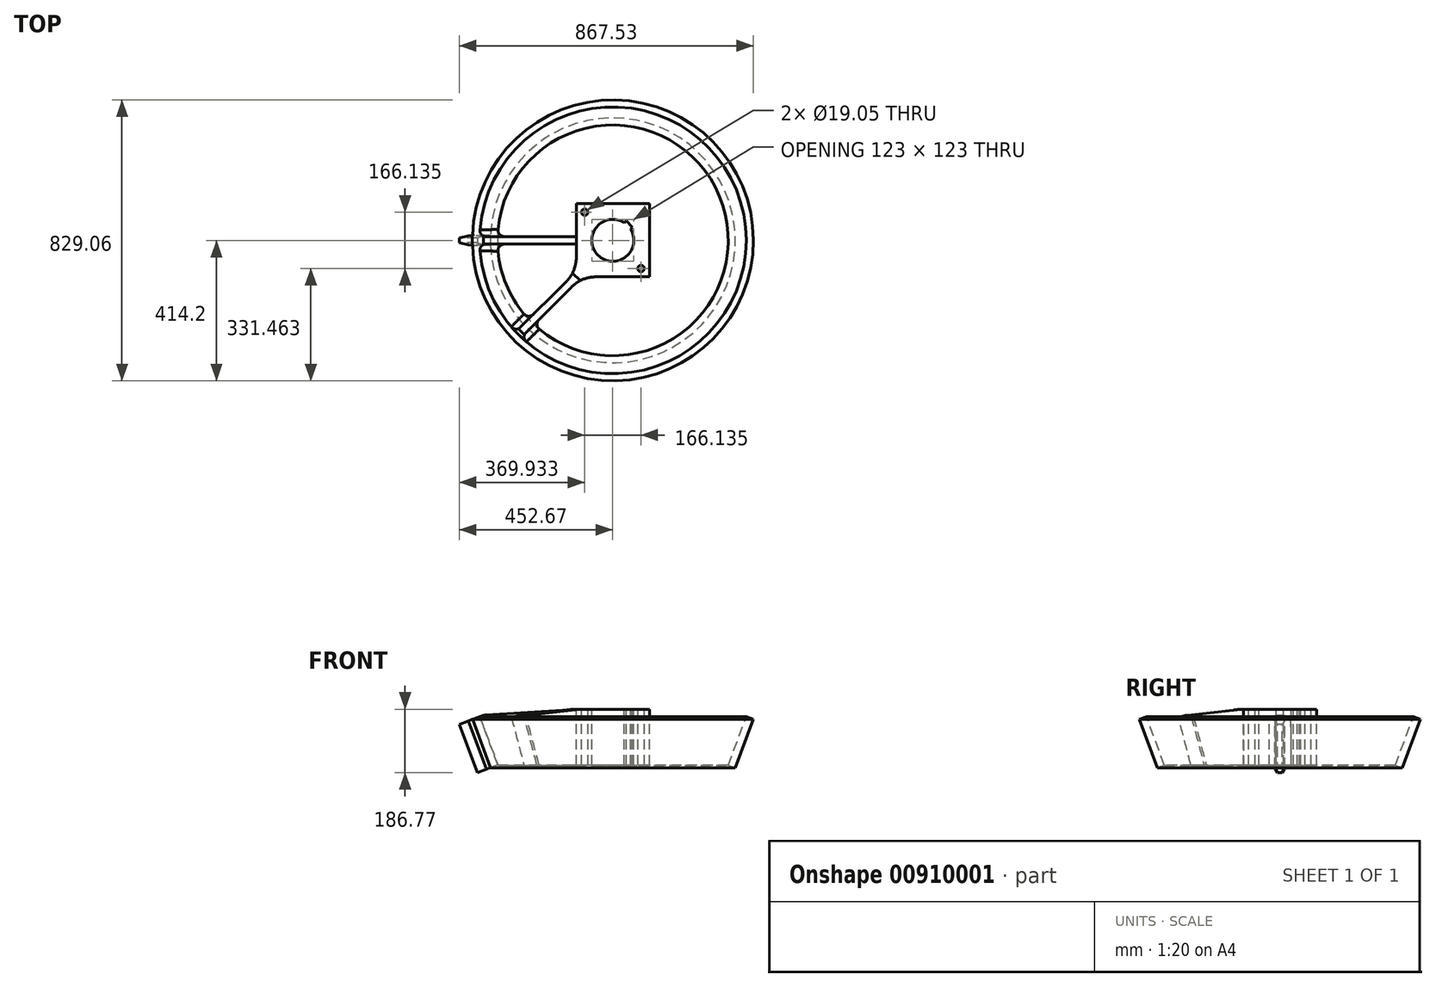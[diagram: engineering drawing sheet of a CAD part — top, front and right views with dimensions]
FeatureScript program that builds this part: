
annotation { "Feature Type Name" : "Feature", "Feature Type Description" : "" }
export const myFeature = defineFeature(function(context is Context, id is Id, definition is map)
    precondition{}
    {
        {
            var Q0;
            Q0=qCreatedBy(makeId("Front.planeOp"),FACE);
            var sketch = newSketch(context, id + "F0", { "sketchPlane" : qUnion([Q0])});
            skLineSegment(sketch, "E0.bottom", {"start": v(107.95, 0) * mm, "end": v(61.91, 0) * mm});
            skLineSegment(sketch, "E0.top", {"start": v(107.95, 165.1) * mm, "end": v(61.91, 165.1) * mm});
            skLineSegment(sketch, "E0.left", {"start": v(107.95, 0) * mm, "end": v(107.95, 165.1) * mm});
            skLineSegment(sketch, "E0.right", {"start": v(-107.95, 0) * mm, "end": v(-107.95, 165.1) * mm});
            skLineSegment(sketch, "E1", {"start": v(61.91, 165.1) * mm, "end": v(61.91, 0) * mm});
            skLineSegment(sketch, "E2", {"start": v(0, 165.1) * mm, "end": v(-107.95, 165.1) * mm});
            skLineSegment(sketch, "E3", {"start": v(61.91, 165.1) * mm, "end": v(0, 165.1) * mm});
            skLineSegment(sketch, "E4", {"start": v(-340.6, 0) * mm, "end": v(-393.7, 142.85) * mm});
            skLineSegment(sketch, "E5", {"start": v(-393.7, 142.85) * mm, "end": v(-414.53, 135.1) * mm});
            skLineSegment(sketch, "E6", {"start": v(-414.53, 135.1) * mm, "end": v(-361.42, -7.75) * mm});
            skLineSegment(sketch, "E7", {"start": v(-361.42, -7.75) * mm, "end": v(-340.6, 0) * mm});
            skLineSegment(sketch, "E8", {"start": v(0, 0) * mm, "end": v(0, 165.1) * mm, "construction": true});
            skLineSegment(sketch, "E9", {"start": v(-340.6, 0) * mm, "end": v(-107.95, 0) * mm});
            skLineSegment(sketch, "E10", {"start": v(-393.7, 142.85) * mm, "end": v(-381.8, 147.27) * mm});
            skLineSegment(sketch, "E11", {"start": v(-381.8, 147.27) * mm, "end": v(-107.95, 165.1) * mm});
            skLineSegment(sketch, "E12", {"start": v(-381.8, 147.27) * mm, "end": v(-386.22, 159.18) * mm});
            skLineSegment(sketch, "E13", {"start": v(-386.22, 159.18) * mm, "end": v(-418.96, 147) * mm});
            skLineSegment(sketch, "E14", {"start": v(-418.96, 147) * mm, "end": v(-414.53, 135.1) * mm});
            skLineSegment(sketch, "E15", {"start": v(-107.95, 0) * mm, "end": v(0, 0) * mm});
            skLineSegment(sketch, "E16", {"start": v(0, 0) * mm, "end": v(61.91, 0) * mm});
            skLineSegment(sketch, "E17", {"start": v(0, 0) * mm, "end": v(0, 165.1) * mm});
            skSolve(sketch);
        }
        {
            var Q0;
            Q0=makeQuery(id+"F0.imprint","IMPRINT",FACE,{"disambiguationData":[TD([[makeQuery(id+"F0.imprint","IMPRINT",EDGE,{"derivedFrom":sQuery(id+"F0.wireOp",EDGE,"E0.right")}),-1.0]])]});
            var Q1;
            Q1=makeQuery(id+"F0.imprint","IMPRINT",FACE,{"disambiguationData":[TD([[makeQuery(id+"F0.imprint","IMPRINT",EDGE,{"derivedFrom":sQuery(id+"F0.wireOp",EDGE,"E1")}),-1.0]])]});
            var Q2;
            Q2=makeQuery(id+"F0.imprint","IMPRINT",FACE,{"disambiguationData":[TD([[makeQuery(id+"F0.imprint","IMPRINT",EDGE,{"derivedFrom":sQuery(id+"F0.wireOp",EDGE,"E0.bottom")}),-1.0]])]});
            extrude(context, id + "F1", {"entities" : qUnion([Q0, Q1, Q2]), "depth" : 215.9 * mm, "offsetDistance" : 25 * mm, "symmetric" : true});
        }
        {
            var Q0;
            Q0=makeQuery(id+"F0.imprint","IMPRINT",FACE,{"disambiguationData":[TD([[makeQuery(id+"F0.imprint","IMPRINT",EDGE,{"derivedFrom":sQuery(id+"F0.wireOp",EDGE,"E0.right")}),1.0]])]});
            extrude(context, id + "F2", {"entities" : qUnion([Q0]), "operationType" : NewBodyOperationType.ADD, "depth" : 22.23 * mm, "offsetDistance" : 25 * mm, "symmetric" : true});
        }
        {
            var Q0;
            Q0=makeQuery(id+"F0.imprint","IMPRINT",FACE,{"disambiguationData":[TD([[makeQuery(id+"F0.imprint","IMPRINT",EDGE,{"derivedFrom":sQuery(id+"F0.wireOp",EDGE,"E4")}),1.0]])]});
            var Q1;
            Q1=sQuery(id+"F0.wireOp",EDGE,"E8");
            revolve(context, id + "F3", {"operationType" : NewBodyOperationType.ADD, "surfaceOperationType" : NewSurfaceOperationType.NEW, "entities" : qUnion([Q0]), "axis" : qUnion([Q1]), "revolveType" : RevolveType.FULL});
        }
        {
            var Q0;
            Q0=makeQuery(id+"F1.opExtrude","CAP_VERTEX",VERTEX,{"disambiguationData":[OSD([sQuery(id+"F0.wireOp",EDGE,"E0.right"),sQuery(id+"F0.wireOp",EDGE,"E2"),sQuery(id+"F0.wireOp",EDGE,"E11")])],"isStart":false});
            var Q1;
            Q1=makeQuery(id+"F1.opExtrude","CAP_VERTEX",VERTEX,{"disambiguationData":[OSD([sQuery(id+"F0.wireOp",EDGE,"E0.right"),sQuery(id+"F0.wireOp",EDGE,"bd23a387-63c8-4da3-bc8b-55db6ce0ce16"),sQuery(id+"F0.wireOp",EDGE,"E9")])],"isStart":false});
            var Q2;
            Q2=makeQuery(id+"F1.opExtrude","CAP_VERTEX",VERTEX,{"disambiguationData":[OSD([sQuery(id+"F0.wireOp",EDGE,"E0.top"),sQuery(id+"F0.wireOp",EDGE,"E0.left")])],"isStart":true});
            cPlane(context, id + "F4", {"entities" : qUnion([Q0, Q1, Q2]), "cplaneType" : CPlaneType.THREE_POINT, "offset" : 25 * mm, "width" : 150 * mm, "height" : 150 * mm});
        }
        {
            var Q0;
            Q0=qCreatedBy(id+"F4.planeOp",FACE);
            var sketch = newSketch(context, id + "F5", { "sketchPlane" : qUnion([Q0])});
            skLineSegment(sketch, "E18", {"start": v(101.86, 165.1) * mm, "end": v(152.66, 165.1) * mm});
            skLineSegment(sketch, "E19", {"start": v(381.8, 146.57) * mm, "end": v(393.7, 142.14) * mm});
            skLineSegment(sketch, "E20", {"start": v(393.7, 142.14) * mm, "end": v(340.85, 0) * mm});
            skLineSegment(sketch, "E21", {"start": v(340.85, 0) * mm, "end": v(101.86, 0) * mm});
            skLineSegment(sketch, "E22", {"start": v(101.86, 0) * mm, "end": v(101.86, 165.1) * mm});
            skLineSegment(sketch, "E23", {"start": v(152.66, 165.1) * mm, "end": v(381.8, 146.57) * mm});
            skSolve(sketch);
        }
        {
            var Q0;
            Q0=makeQuery(id+"F5.imprint","IMPRINT",FACE,{"disambiguationData":[TD([[makeQuery(id+"F5.imprint","IMPRINT",EDGE,{"derivedFrom":sQuery(id+"F5.wireOp",EDGE,"E18")}),-1.0]])]});
            extrude(context, id + "F6", {"entities" : qUnion([Q0]), "operationType" : NewBodyOperationType.ADD, "depth" : 22.23 * mm, "offsetDistance" : 25 * mm, "symmetric" : true});
        }
        {
            var Q0;
            Q0=makeQuery(id+"F2.opExtrude","CAP_EDGE",EDGE,{"disambiguationData":[OSD([sQuery(id+"F0.wireOp",EDGE,"E0.right")])],"isStart":false});
            var Q1;
            Q1=makeQuery(id+"F2.opExtrude","CAP_EDGE",EDGE,{"disambiguationData":[OSD([sQuery(id+"F0.wireOp",EDGE,"E0.right")])],"isStart":true});
            var Q2;
            {var subQ0=sQuery(id+"F0.wireOp",EDGE,"E4");Q2=makeQuery(id+"F3.boolean.opBoolean","INTERSECT",EDGE,{"derivedFrom":[makeQuery(id+"F2.opExtrude","CAP_FACE",FACE,{"disambiguationData":[OSD([sQuery(id+"F0.wireOp",EDGE,"E0.right"),subQ0,sQuery(id+"F0.wireOp",EDGE,"E9"),sQuery(id+"F0.wireOp",EDGE,"E10"),sQuery(id+"F0.wireOp",EDGE,"E11")])],"isStart":true}),makeQuery(id+"F3.opRevolve","SWEPT_FACE",FACE,{"disambiguationData":[OSD([subQ0])]})]});}
            var Q3;
            {var subQ0=sQuery(id+"F0.wireOp",EDGE,"E4");Q3=makeQuery(id+"F3.boolean.opBoolean","INTERSECT",EDGE,{"derivedFrom":[makeQuery(id+"F2.opExtrude","CAP_FACE",FACE,{"disambiguationData":[OSD([sQuery(id+"F0.wireOp",EDGE,"E0.right"),subQ0,sQuery(id+"F0.wireOp",EDGE,"E9"),sQuery(id+"F0.wireOp",EDGE,"E10"),sQuery(id+"F0.wireOp",EDGE,"E11")])],"isStart":false}),makeQuery(id+"F3.opRevolve","SWEPT_FACE",FACE,{"disambiguationData":[OSD([subQ0])]})]});}
            var Q4;
            Q4=makeQuery(id+"F6.boolean.opBoolean","INTERSECT",EDGE,{"derivedFrom":[makeQuery(id+"F3.opRevolve","SWEPT_FACE",FACE,{"disambiguationData":[OSD([sQuery(id+"F0.wireOp",EDGE,"E4")])]}),makeQuery(id+"F6.opExtrude","CAP_FACE",FACE,{"disambiguationData":[OSD([sQuery(id+"F5.wireOp",EDGE,"E18"),sQuery(id+"F5.wireOp",EDGE,"E19"),sQuery(id+"F5.wireOp",EDGE,"E20"),sQuery(id+"F5.wireOp",EDGE,"E21"),sQuery(id+"F5.wireOp",EDGE,"E22"),sQuery(id+"F5.wireOp",EDGE,"E23")])],"isStart":false})]});
            var Q5;
            Q5=makeQuery(id+"F6.boolean.opBoolean","INTERSECT",EDGE,{"derivedFrom":[makeQuery(id+"F3.opRevolve","SWEPT_FACE",FACE,{"disambiguationData":[OSD([sQuery(id+"F0.wireOp",EDGE,"E4")])]}),makeQuery(id+"F6.opExtrude","CAP_FACE",FACE,{"disambiguationData":[OSD([sQuery(id+"F5.wireOp",EDGE,"E18"),sQuery(id+"F5.wireOp",EDGE,"E19"),sQuery(id+"F5.wireOp",EDGE,"E20"),sQuery(id+"F5.wireOp",EDGE,"E21"),sQuery(id+"F5.wireOp",EDGE,"E22"),sQuery(id+"F5.wireOp",EDGE,"E23")])],"isStart":true})]});
            var Q6;
            {var subQ0=sQuery(id+"F5.wireOp",EDGE,"E21");var subQ2=sQuery(id+"F0.wireOp",EDGE,"E9");var subQ9=sQuery(id+"F0.wireOp",EDGE,"E11");var subQ10=sQuery(id+"F0.wireOp",EDGE,"E10");var subQ11=sQuery(id+"F0.wireOp",EDGE,"E4");var subQ12=sQuery(id+"F0.wireOp",EDGE,"E0.right");var subQ13=makeQuery(id+"F2.opExtrude","CAP_FACE",FACE,{"disambiguationData":[OSD([subQ12,subQ11,subQ2,subQ10,subQ9])],"isStart":true});Q6=makeQuery(id+"FeQxwqO8TE0xPhn_1.3.F6.boolean.opBoolean","INTERSECT",EDGE,{"derivedFrom":[makeQuery(id+"FeQxwqO8TE0xPhn_1.3.F2.boolean.opBoolean","SPLIT",FACE,{"disambiguationData":[TD([subQ13])],"derivedFrom":makeQuery(id+"FeQxwqO8TE0xPhn_1.2.F2.boolean.opBoolean","SPLIT",FACE,{"disambiguationData":[TD([subQ13])],"derivedFrom":makeQuery(id+"FeQxwqO8TE0xPhn_1.1.F2.boolean.opBoolean","SPLIT",FACE,{"disambiguationData":[TD([subQ13])],"derivedFrom":makeQuery(id+"F3.opRevolve","SWEPT_FACE",FACE,{"disambiguationData":[OSD([subQ11])]})})})}),makeQuery(id+"FeQxwqO8TE0xPhn_1.3.F6.opExtrude","CAP_FACE",FACE,{"disambiguationData":[OSD([sQuery(id+"F5.wireOp",EDGE,"E18"),sQuery(id+"F5.wireOp",EDGE,"E19"),sQuery(id+"F5.wireOp",EDGE,"E20"),subQ0,sQuery(id+"F5.wireOp",EDGE,"E22"),sQuery(id+"F5.wireOp",EDGE,"E23")])],"isStart":true})]});}
            var Q7;
            {var subQ0=sQuery(id+"F5.wireOp",EDGE,"E21");var subQ2=sQuery(id+"F0.wireOp",EDGE,"E9");var subQ9=sQuery(id+"F0.wireOp",EDGE,"E11");var subQ10=sQuery(id+"F0.wireOp",EDGE,"E10");var subQ11=sQuery(id+"F0.wireOp",EDGE,"E4");var subQ12=sQuery(id+"F0.wireOp",EDGE,"E0.right");var subQ13=makeQuery(id+"F2.opExtrude","CAP_FACE",FACE,{"disambiguationData":[OSD([subQ12,subQ11,subQ2,subQ10,subQ9])],"isStart":true});Q7=makeQuery(id+"FeQxwqO8TE0xPhn_1.3.F6.boolean.opBoolean","INTERSECT",EDGE,{"derivedFrom":[makeQuery(id+"FeQxwqO8TE0xPhn_1.3.F2.boolean.opBoolean","SPLIT",FACE,{"disambiguationData":[TD([subQ13])],"derivedFrom":makeQuery(id+"FeQxwqO8TE0xPhn_1.2.F2.boolean.opBoolean","SPLIT",FACE,{"disambiguationData":[TD([subQ13])],"derivedFrom":makeQuery(id+"FeQxwqO8TE0xPhn_1.1.F2.boolean.opBoolean","SPLIT",FACE,{"disambiguationData":[TD([subQ13])],"derivedFrom":makeQuery(id+"F3.opRevolve","SWEPT_FACE",FACE,{"disambiguationData":[OSD([subQ11])]})})})}),makeQuery(id+"FeQxwqO8TE0xPhn_1.3.F6.opExtrude","CAP_FACE",FACE,{"disambiguationData":[OSD([sQuery(id+"F5.wireOp",EDGE,"E18"),sQuery(id+"F5.wireOp",EDGE,"E19"),sQuery(id+"F5.wireOp",EDGE,"E20"),subQ0,sQuery(id+"F5.wireOp",EDGE,"E22"),sQuery(id+"F5.wireOp",EDGE,"E23")])],"isStart":false})]});}
            var Q8;
            {var subQ0=sQuery(id+"F0.wireOp",EDGE,"E11");var subQ1=sQuery(id+"F0.wireOp",EDGE,"E10");var subQ2=sQuery(id+"F0.wireOp",EDGE,"E9");var subQ3=sQuery(id+"F0.wireOp",EDGE,"E4");var subQ4=sQuery(id+"F0.wireOp",EDGE,"E0.right");var subQ6=makeQuery(id+"F2.opExtrude","CAP_FACE",FACE,{"disambiguationData":[OSD([subQ4,subQ3,subQ2,subQ1,subQ0])],"isStart":true});Q8=makeQuery(id+"FeQxwqO8TE0xPhn_1.3.F2.boolean.opBoolean","INTERSECT",EDGE,{"derivedFrom":[makeQuery(id+"FeQxwqO8TE0xPhn_1.2.F2.boolean.opBoolean","SPLIT",FACE,{"disambiguationData":[TD([subQ6])],"derivedFrom":makeQuery(id+"FeQxwqO8TE0xPhn_1.1.F2.boolean.opBoolean","SPLIT",FACE,{"disambiguationData":[TD([subQ6])],"derivedFrom":makeQuery(id+"F3.opRevolve","SWEPT_FACE",FACE,{"disambiguationData":[OSD([subQ3])]})})}),makeQuery(id+"FeQxwqO8TE0xPhn_1.3.F2.opExtrude","CAP_FACE",FACE,{"disambiguationData":[OSD([subQ4,subQ3,subQ2,subQ1,subQ0])],"isStart":false})]});}
            var Q9;
            {var subQ0=sQuery(id+"F0.wireOp",EDGE,"E11");var subQ1=sQuery(id+"F0.wireOp",EDGE,"E10");var subQ2=sQuery(id+"F0.wireOp",EDGE,"E9");var subQ3=sQuery(id+"F0.wireOp",EDGE,"E4");var subQ4=sQuery(id+"F0.wireOp",EDGE,"E0.right");var subQ6=makeQuery(id+"F2.opExtrude","CAP_FACE",FACE,{"disambiguationData":[OSD([subQ4,subQ3,subQ2,subQ1,subQ0])],"isStart":true});Q9=makeQuery(id+"FeQxwqO8TE0xPhn_1.3.F2.boolean.opBoolean","INTERSECT",EDGE,{"derivedFrom":[makeQuery(id+"FeQxwqO8TE0xPhn_1.2.F2.boolean.opBoolean","SPLIT",FACE,{"disambiguationData":[TD([subQ6])],"derivedFrom":makeQuery(id+"FeQxwqO8TE0xPhn_1.1.F2.boolean.opBoolean","SPLIT",FACE,{"disambiguationData":[TD([subQ6])],"derivedFrom":makeQuery(id+"F3.opRevolve","SWEPT_FACE",FACE,{"disambiguationData":[OSD([subQ3])]})})}),makeQuery(id+"FeQxwqO8TE0xPhn_1.3.F2.opExtrude","CAP_FACE",FACE,{"disambiguationData":[OSD([subQ4,subQ3,subQ2,subQ1,subQ0])],"isStart":true})]});}
            var Q10;
            Q10=makeQuery(id+"FeQxwqO8TE0xPhn_1.3.F2.opExtrude","CAP_EDGE",EDGE,{"disambiguationData":[OSD([sQuery(id+"F0.wireOp",EDGE,"E0.right")])],"isStart":true});
            var Q11;
            Q11=makeQuery(id+"FeQxwqO8TE0xPhn_1.3.F2.opExtrude","CAP_EDGE",EDGE,{"disambiguationData":[OSD([sQuery(id+"F0.wireOp",EDGE,"E0.right")])],"isStart":false});
            var Q12;
            {var subQ0=sQuery(id+"F5.wireOp",EDGE,"E21");var subQ2=sQuery(id+"F0.wireOp",EDGE,"E11");var subQ3=sQuery(id+"F0.wireOp",EDGE,"E10");var subQ4=sQuery(id+"F0.wireOp",EDGE,"E9");var subQ5=sQuery(id+"F0.wireOp",EDGE,"E4");var subQ6=sQuery(id+"F0.wireOp",EDGE,"E0.right");var subQ7=makeQuery(id+"F2.opExtrude","CAP_FACE",FACE,{"disambiguationData":[OSD([subQ6,subQ5,subQ4,subQ3,subQ2])],"isStart":true});Q12=makeQuery(id+"FeQxwqO8TE0xPhn_1.2.F6.boolean.opBoolean","INTERSECT",EDGE,{"derivedFrom":[makeQuery(id+"FeQxwqO8TE0xPhn_1.2.F2.boolean.opBoolean","SPLIT",FACE,{"disambiguationData":[TD([subQ7])],"derivedFrom":makeQuery(id+"FeQxwqO8TE0xPhn_1.1.F2.boolean.opBoolean","SPLIT",FACE,{"disambiguationData":[TD([subQ7])],"derivedFrom":makeQuery(id+"F3.opRevolve","SWEPT_FACE",FACE,{"disambiguationData":[OSD([subQ5])]})})}),makeQuery(id+"FeQxwqO8TE0xPhn_1.2.F6.opExtrude","CAP_FACE",FACE,{"disambiguationData":[OSD([sQuery(id+"F5.wireOp",EDGE,"E18"),sQuery(id+"F5.wireOp",EDGE,"E19"),sQuery(id+"F5.wireOp",EDGE,"E20"),subQ0,sQuery(id+"F5.wireOp",EDGE,"E22"),sQuery(id+"F5.wireOp",EDGE,"E23")])],"isStart":true})]});}
            var Q13;
            {var subQ0=sQuery(id+"F5.wireOp",EDGE,"E21");var subQ2=sQuery(id+"F0.wireOp",EDGE,"E11");var subQ3=sQuery(id+"F0.wireOp",EDGE,"E10");var subQ4=sQuery(id+"F0.wireOp",EDGE,"E9");var subQ5=sQuery(id+"F0.wireOp",EDGE,"E4");var subQ6=sQuery(id+"F0.wireOp",EDGE,"E0.right");var subQ7=makeQuery(id+"F2.opExtrude","CAP_FACE",FACE,{"disambiguationData":[OSD([subQ6,subQ5,subQ4,subQ3,subQ2])],"isStart":true});Q13=makeQuery(id+"FeQxwqO8TE0xPhn_1.2.F6.boolean.opBoolean","INTERSECT",EDGE,{"derivedFrom":[makeQuery(id+"FeQxwqO8TE0xPhn_1.2.F2.boolean.opBoolean","SPLIT",FACE,{"disambiguationData":[TD([subQ7])],"derivedFrom":makeQuery(id+"FeQxwqO8TE0xPhn_1.1.F2.boolean.opBoolean","SPLIT",FACE,{"disambiguationData":[TD([subQ7])],"derivedFrom":makeQuery(id+"F3.opRevolve","SWEPT_FACE",FACE,{"disambiguationData":[OSD([subQ5])]})})}),makeQuery(id+"FeQxwqO8TE0xPhn_1.2.F6.opExtrude","CAP_FACE",FACE,{"disambiguationData":[OSD([sQuery(id+"F5.wireOp",EDGE,"E18"),sQuery(id+"F5.wireOp",EDGE,"E19"),sQuery(id+"F5.wireOp",EDGE,"E20"),subQ0,sQuery(id+"F5.wireOp",EDGE,"E22"),sQuery(id+"F5.wireOp",EDGE,"E23")])],"isStart":false})]});}
            var Q14;
            Q14=makeQuery(id+"FeQxwqO8TE0xPhn_1.2.F2.opExtrude","CAP_EDGE",EDGE,{"disambiguationData":[OSD([sQuery(id+"F0.wireOp",EDGE,"E0.right")])],"isStart":false});
            var Q15;
            {var subQ0=sQuery(id+"F0.wireOp",EDGE,"E11");var subQ1=sQuery(id+"F0.wireOp",EDGE,"E10");var subQ2=sQuery(id+"F0.wireOp",EDGE,"E9");var subQ3=sQuery(id+"F0.wireOp",EDGE,"E4");var subQ4=sQuery(id+"F0.wireOp",EDGE,"E0.right");Q15=makeQuery(id+"FeQxwqO8TE0xPhn_1.2.F2.boolean.opBoolean","INTERSECT",EDGE,{"derivedFrom":[makeQuery(id+"FeQxwqO8TE0xPhn_1.1.F2.boolean.opBoolean","SPLIT",FACE,{"disambiguationData":[TD([makeQuery(id+"F2.opExtrude","CAP_FACE",FACE,{"disambiguationData":[OSD([subQ4,subQ3,subQ2,subQ1,subQ0])],"isStart":true})])],"derivedFrom":makeQuery(id+"F3.opRevolve","SWEPT_FACE",FACE,{"disambiguationData":[OSD([subQ3])]})}),makeQuery(id+"FeQxwqO8TE0xPhn_1.2.F2.opExtrude","CAP_FACE",FACE,{"disambiguationData":[OSD([subQ4,subQ3,subQ2,subQ1,subQ0])],"isStart":false})]});}
            var Q16;
            Q16=makeQuery(id+"FeQxwqO8TE0xPhn_1.2.F2.opExtrude","CAP_EDGE",EDGE,{"disambiguationData":[OSD([sQuery(id+"F0.wireOp",EDGE,"E0.right")])],"isStart":true});
            var Q17;
            Q17=makeQuery(id+"FeQxwqO8TE0xPhn_1.1.F2.opExtrude","CAP_EDGE",EDGE,{"disambiguationData":[OSD([sQuery(id+"F0.wireOp",EDGE,"E0.right")])],"isStart":false});
            var Q18;
            Q18=makeQuery(id+"FeQxwqO8TE0xPhn_1.1.F2.opExtrude","CAP_EDGE",EDGE,{"disambiguationData":[OSD([sQuery(id+"F0.wireOp",EDGE,"E0.right")])],"isStart":true});
            var Q19;
            {var subQ0=sQuery(id+"F0.wireOp",EDGE,"E4");Q19=makeQuery(id+"FeQxwqO8TE0xPhn_1.1.F2.boolean.opBoolean","INTERSECT",EDGE,{"derivedFrom":[makeQuery(id+"F3.opRevolve","SWEPT_FACE",FACE,{"disambiguationData":[OSD([subQ0])]}),makeQuery(id+"FeQxwqO8TE0xPhn_1.1.F2.opExtrude","CAP_FACE",FACE,{"disambiguationData":[OSD([sQuery(id+"F0.wireOp",EDGE,"E0.right"),subQ0,sQuery(id+"F0.wireOp",EDGE,"E9"),sQuery(id+"F0.wireOp",EDGE,"E10"),sQuery(id+"F0.wireOp",EDGE,"E11")])],"isStart":true})]});}
            var Q20;
            {var subQ0=sQuery(id+"F5.wireOp",EDGE,"E21");var subQ1=sQuery(id+"F0.wireOp",EDGE,"E11");var subQ2=sQuery(id+"F0.wireOp",EDGE,"E10");var subQ3=sQuery(id+"F0.wireOp",EDGE,"E9");var subQ4=sQuery(id+"F0.wireOp",EDGE,"E4");var subQ5=sQuery(id+"F0.wireOp",EDGE,"E0.right");Q20=makeQuery(id+"FeQxwqO8TE0xPhn_1.1.F6.boolean.opBoolean","INTERSECT",EDGE,{"derivedFrom":[makeQuery(id+"FeQxwqO8TE0xPhn_1.1.F2.boolean.opBoolean","SPLIT",FACE,{"disambiguationData":[TD([makeQuery(id+"F2.opExtrude","CAP_FACE",FACE,{"disambiguationData":[OSD([subQ5,subQ4,subQ3,subQ2,subQ1])],"isStart":true})])],"derivedFrom":makeQuery(id+"F3.opRevolve","SWEPT_FACE",FACE,{"disambiguationData":[OSD([subQ4])]})}),makeQuery(id+"FeQxwqO8TE0xPhn_1.1.F6.opExtrude","CAP_FACE",FACE,{"disambiguationData":[OSD([sQuery(id+"F5.wireOp",EDGE,"E18"),sQuery(id+"F5.wireOp",EDGE,"E19"),sQuery(id+"F5.wireOp",EDGE,"E20"),subQ0,sQuery(id+"F5.wireOp",EDGE,"E22"),sQuery(id+"F5.wireOp",EDGE,"E23")])],"isStart":false})]});}
            var Q21;
            {var subQ0=sQuery(id+"F0.wireOp",EDGE,"E11");var subQ1=sQuery(id+"F0.wireOp",EDGE,"E10");var subQ2=sQuery(id+"F0.wireOp",EDGE,"E9");var subQ3=sQuery(id+"F0.wireOp",EDGE,"E4");var subQ4=sQuery(id+"F0.wireOp",EDGE,"E0.right");Q21=makeQuery(id+"FeQxwqO8TE0xPhn_1.2.F2.boolean.opBoolean","INTERSECT",EDGE,{"derivedFrom":[makeQuery(id+"FeQxwqO8TE0xPhn_1.1.F2.boolean.opBoolean","SPLIT",FACE,{"disambiguationData":[TD([makeQuery(id+"F2.opExtrude","CAP_FACE",FACE,{"disambiguationData":[OSD([subQ4,subQ3,subQ2,subQ1,subQ0])],"isStart":true})])],"derivedFrom":makeQuery(id+"F3.opRevolve","SWEPT_FACE",FACE,{"disambiguationData":[OSD([subQ3])]})}),makeQuery(id+"FeQxwqO8TE0xPhn_1.2.F2.opExtrude","CAP_FACE",FACE,{"disambiguationData":[OSD([subQ4,subQ3,subQ2,subQ1,subQ0])],"isStart":true})]});}
            var Q22;
            {var subQ0=sQuery(id+"F5.wireOp",EDGE,"E21");var subQ1=sQuery(id+"F0.wireOp",EDGE,"E11");var subQ2=sQuery(id+"F0.wireOp",EDGE,"E10");var subQ3=sQuery(id+"F0.wireOp",EDGE,"E9");var subQ4=sQuery(id+"F0.wireOp",EDGE,"E4");var subQ5=sQuery(id+"F0.wireOp",EDGE,"E0.right");Q22=makeQuery(id+"FeQxwqO8TE0xPhn_1.1.F6.boolean.opBoolean","INTERSECT",EDGE,{"derivedFrom":[makeQuery(id+"FeQxwqO8TE0xPhn_1.1.F2.boolean.opBoolean","SPLIT",FACE,{"disambiguationData":[TD([makeQuery(id+"F2.opExtrude","CAP_FACE",FACE,{"disambiguationData":[OSD([subQ5,subQ4,subQ3,subQ2,subQ1])],"isStart":true})])],"derivedFrom":makeQuery(id+"F3.opRevolve","SWEPT_FACE",FACE,{"disambiguationData":[OSD([subQ4])]})}),makeQuery(id+"FeQxwqO8TE0xPhn_1.1.F6.opExtrude","CAP_FACE",FACE,{"disambiguationData":[OSD([sQuery(id+"F5.wireOp",EDGE,"E18"),sQuery(id+"F5.wireOp",EDGE,"E19"),sQuery(id+"F5.wireOp",EDGE,"E20"),subQ0,sQuery(id+"F5.wireOp",EDGE,"E22"),sQuery(id+"F5.wireOp",EDGE,"E23")])],"isStart":true})]});}
            var Q23;
            {var subQ0=sQuery(id+"F0.wireOp",EDGE,"E4");Q23=makeQuery(id+"FeQxwqO8TE0xPhn_1.1.F2.boolean.opBoolean","INTERSECT",EDGE,{"derivedFrom":[makeQuery(id+"F3.opRevolve","SWEPT_FACE",FACE,{"disambiguationData":[OSD([subQ0])]}),makeQuery(id+"FeQxwqO8TE0xPhn_1.1.F2.opExtrude","CAP_FACE",FACE,{"disambiguationData":[OSD([sQuery(id+"F0.wireOp",EDGE,"E0.right"),subQ0,sQuery(id+"F0.wireOp",EDGE,"E9"),sQuery(id+"F0.wireOp",EDGE,"E10"),sQuery(id+"F0.wireOp",EDGE,"E11")])],"isStart":false})]});}
            fillet(context, id + "F7", {"entities" : qUnion([Q0, Q1, Q2, Q3, Q4, Q5, Q6, Q7, Q8, Q9, Q10, Q11, Q12, Q13, Q14, Q15, Q16, Q17, Q18, Q19, Q20, Q21, Q22, Q23]), "radius" : 19.05 * mm, "tangentPropagation" : true, "allowEdgeOverflow" : false});
        }
        {
            var Q0;
            Q0=makeQuery(id+"F6.boolean.opBoolean","INTERSECT",EDGE,{"derivedFrom":[makeQuery(id+"F1.opExtrude","CAP_FACE",FACE,{"disambiguationData":[OSD([sQuery(id+"F0.wireOp",EDGE,"E0.bottom"),sQuery(id+"F0.wireOp",EDGE,"E0.top"),sQuery(id+"F0.wireOp",EDGE,"E0.left"),sQuery(id+"F0.wireOp",EDGE,"E0.right"),sQuery(id+"F0.wireOp",EDGE,"E2"),sQuery(id+"F0.wireOp",EDGE,"E3"),sQuery(id+"F0.wireOp",EDGE,"16a788df-045e-4882-b183-54f5a1eef0ef"),sQuery(id+"F0.wireOp",EDGE,"bd23a387-63c8-4da3-bc8b-55db6ce0ce16")])],"isStart":false}),makeQuery(id+"F6.opExtrude","CAP_FACE",FACE,{"disambiguationData":[OSD([sQuery(id+"F5.wireOp",EDGE,"E18"),sQuery(id+"F5.wireOp",EDGE,"E19"),sQuery(id+"F5.wireOp",EDGE,"E20"),sQuery(id+"F5.wireOp",EDGE,"E21"),sQuery(id+"F5.wireOp",EDGE,"E22"),sQuery(id+"F5.wireOp",EDGE,"E23")])],"isStart":true})]});
            var Q1;
            {var subQ0=sQuery(id+"F0.wireOp",EDGE,"E11");var subQ1=sQuery(id+"F0.wireOp",EDGE,"E9");var subQ2=sQuery(id+"F0.wireOp",EDGE,"E0.right");Q1=makeQuery(id+"F6.boolean.opBoolean","INTERSECT",EDGE,{"derivedFrom":[makeQuery(id+"F2.boolean.opBoolean","SPLIT",FACE,{"disambiguationData":[TD([makeQuery(id+"F2.opExtrude","CAP_FACE",FACE,{"disambiguationData":[OSD([subQ2,sQuery(id+"F0.wireOp",EDGE,"E4"),subQ1,sQuery(id+"F0.wireOp",EDGE,"E10"),subQ0])],"isStart":false})])],"derivedFrom":makeQuery(id+"F1.opExtrude","SWEPT_FACE",FACE,{"disambiguationData":[OSD([subQ2])]})}),makeQuery(id+"F6.opExtrude","CAP_FACE",FACE,{"disambiguationData":[OSD([sQuery(id+"F5.wireOp",EDGE,"E18"),sQuery(id+"F5.wireOp",EDGE,"E19"),sQuery(id+"F5.wireOp",EDGE,"E20"),sQuery(id+"F5.wireOp",EDGE,"E21"),sQuery(id+"F5.wireOp",EDGE,"E22"),sQuery(id+"F5.wireOp",EDGE,"E23")])],"isStart":false})]});}
            var Q2;
            {var subQ0=sQuery(id+"F0.wireOp",EDGE,"E11");var subQ1=sQuery(id+"F0.wireOp",EDGE,"E9");var subQ2=sQuery(id+"F0.wireOp",EDGE,"E0.right");Q2=makeQuery(id+"FeQxwqO8TE0xPhn_1.3.F6.boolean.opBoolean","INTERSECT",EDGE,{"derivedFrom":[makeQuery(id+"F2.boolean.opBoolean","SPLIT",FACE,{"disambiguationData":[TD([makeQuery(id+"F2.opExtrude","CAP_FACE",FACE,{"disambiguationData":[OSD([subQ2,sQuery(id+"F0.wireOp",EDGE,"E4"),subQ1,sQuery(id+"F0.wireOp",EDGE,"E10"),subQ0])],"isStart":true})])],"derivedFrom":makeQuery(id+"F1.opExtrude","SWEPT_FACE",FACE,{"disambiguationData":[OSD([subQ2])]})}),makeQuery(id+"FeQxwqO8TE0xPhn_1.3.F6.opExtrude","CAP_FACE",FACE,{"disambiguationData":[OSD([sQuery(id+"F5.wireOp",EDGE,"E18"),sQuery(id+"F5.wireOp",EDGE,"E19"),sQuery(id+"F5.wireOp",EDGE,"E20"),sQuery(id+"F5.wireOp",EDGE,"E21"),sQuery(id+"F5.wireOp",EDGE,"E22"),sQuery(id+"F5.wireOp",EDGE,"E23")])],"isStart":true})]});}
            var Q3;
            {var subQ0=sQuery(id+"F5.wireOp",EDGE,"E21");var subQ1=sQuery(id+"F5.wireOp",EDGE,"E18");var subQ3=sQuery(id+"F0.wireOp",EDGE,"E3");var subQ4=sQuery(id+"F0.wireOp",EDGE,"E2");var subQ5=sQuery(id+"F0.wireOp",EDGE,"E0.top");var subQ7=sQuery(id+"F0.wireOp",EDGE,"E0.right");var subQ8=sQuery(id+"F0.wireOp",EDGE,"bd23a387-63c8-4da3-bc8b-55db6ce0ce16");var subQ9=sQuery(id+"F0.wireOp",EDGE,"16a788df-045e-4882-b183-54f5a1eef0ef");var subQ10=sQuery(id+"F0.wireOp",EDGE,"E0.bottom");Q3=makeQuery(id+"FeQxwqO8TE0xPhn_1.3.F6.boolean.opBoolean","INTERSECT",EDGE,{"derivedFrom":[makeQuery(id+"FeQxwqO8TE0xPhn_1.3.F2.boolean.opBoolean","SPLIT",FACE,{"disambiguationData":[TD([makeQuery(id+"F1.opExtrude","SWEPT_FACE",FACE,{"disambiguationData":[OSD([subQ7])]})])],"derivedFrom":makeQuery(id+"F1.opExtrude","CAP_FACE",FACE,{"disambiguationData":[OSD([subQ10,subQ5,sQuery(id+"F0.wireOp",EDGE,"E0.left"),subQ7,subQ4,subQ3,subQ9,subQ8])],"isStart":true})}),makeQuery(id+"FeQxwqO8TE0xPhn_1.3.F6.opExtrude","CAP_FACE",FACE,{"disambiguationData":[OSD([subQ1,sQuery(id+"F5.wireOp",EDGE,"E19"),sQuery(id+"F5.wireOp",EDGE,"E20"),subQ0,sQuery(id+"F5.wireOp",EDGE,"E22"),sQuery(id+"F5.wireOp",EDGE,"E23")])],"isStart":false})]});}
            var Q4;
            Q4=makeQuery(id+"FeQxwqO8TE0xPhn_1.2.F6.boolean.opBoolean","INTERSECT",EDGE,{"derivedFrom":[makeQuery(id+"F1.opExtrude","CAP_FACE",FACE,{"disambiguationData":[OSD([sQuery(id+"F0.wireOp",EDGE,"E0.bottom"),sQuery(id+"F0.wireOp",EDGE,"E0.top"),sQuery(id+"F0.wireOp",EDGE,"E0.left"),sQuery(id+"F0.wireOp",EDGE,"E0.right"),sQuery(id+"F0.wireOp",EDGE,"E2"),sQuery(id+"F0.wireOp",EDGE,"E3"),sQuery(id+"F0.wireOp",EDGE,"16a788df-045e-4882-b183-54f5a1eef0ef"),sQuery(id+"F0.wireOp",EDGE,"bd23a387-63c8-4da3-bc8b-55db6ce0ce16")])],"isStart":true}),makeQuery(id+"FeQxwqO8TE0xPhn_1.2.F6.opExtrude","CAP_FACE",FACE,{"disambiguationData":[OSD([sQuery(id+"F5.wireOp",EDGE,"E18"),sQuery(id+"F5.wireOp",EDGE,"E19"),sQuery(id+"F5.wireOp",EDGE,"E20"),sQuery(id+"F5.wireOp",EDGE,"E21"),sQuery(id+"F5.wireOp",EDGE,"E22"),sQuery(id+"F5.wireOp",EDGE,"E23")])],"isStart":true})]});
            var Q5;
            {var subQ0=sQuery(id+"F5.wireOp",EDGE,"E21");var subQ1=sQuery(id+"F5.wireOp",EDGE,"E18");var subQ2=sQuery(id+"F0.wireOp",EDGE,"E9");var subQ6=sQuery(id+"F0.wireOp",EDGE,"E11");var subQ7=sQuery(id+"F0.wireOp",EDGE,"E0.right");var subQ10=sQuery(id+"F0.wireOp",EDGE,"E0.left");Q5=makeQuery(id+"FeQxwqO8TE0xPhn_1.2.F6.boolean.opBoolean","INTERSECT",EDGE,{"derivedFrom":[makeQuery(id+"FeQxwqO8TE0xPhn_1.2.F2.boolean.opBoolean","SPLIT",FACE,{"disambiguationData":[TD([makeQuery(id+"FeQxwqO8TE0xPhn_1.2.F2.opExtrude","CAP_FACE",FACE,{"disambiguationData":[OSD([subQ7,sQuery(id+"F0.wireOp",EDGE,"E4"),subQ2,sQuery(id+"F0.wireOp",EDGE,"E10"),subQ6])],"isStart":false})])],"derivedFrom":makeQuery(id+"F1.opExtrude","SWEPT_FACE",FACE,{"disambiguationData":[OSD([subQ10])]})}),makeQuery(id+"FeQxwqO8TE0xPhn_1.2.F6.opExtrude","CAP_FACE",FACE,{"disambiguationData":[OSD([subQ1,sQuery(id+"F5.wireOp",EDGE,"E19"),sQuery(id+"F5.wireOp",EDGE,"E20"),subQ0,sQuery(id+"F5.wireOp",EDGE,"E22"),sQuery(id+"F5.wireOp",EDGE,"E23")])],"isStart":false})]});}
            var Q6;
            Q6=makeQuery(id+"FeQxwqO8TE0xPhn_1.1.F6.boolean.opBoolean","INTERSECT",EDGE,{"derivedFrom":[makeQuery(id+"F1.opExtrude","SWEPT_FACE",FACE,{"disambiguationData":[OSD([sQuery(id+"F0.wireOp",EDGE,"E0.left")])]}),makeQuery(id+"FeQxwqO8TE0xPhn_1.1.F6.opExtrude","CAP_FACE",FACE,{"disambiguationData":[OSD([sQuery(id+"F5.wireOp",EDGE,"E18"),sQuery(id+"F5.wireOp",EDGE,"E19"),sQuery(id+"F5.wireOp",EDGE,"E20"),sQuery(id+"F5.wireOp",EDGE,"E21"),sQuery(id+"F5.wireOp",EDGE,"E22"),sQuery(id+"F5.wireOp",EDGE,"E23")])],"isStart":true})]});
            var Q7;
            {var subQ0=sQuery(id+"F5.wireOp",EDGE,"E21");var subQ1=sQuery(id+"F5.wireOp",EDGE,"E18");var subQ2=sQuery(id+"F0.wireOp",EDGE,"E0.left");var subQ3=sQuery(id+"F0.wireOp",EDGE,"E3");var subQ4=sQuery(id+"F0.wireOp",EDGE,"E2");var subQ5=sQuery(id+"F0.wireOp",EDGE,"E0.top");var subQ7=sQuery(id+"F0.wireOp",EDGE,"bd23a387-63c8-4da3-bc8b-55db6ce0ce16");var subQ8=sQuery(id+"F0.wireOp",EDGE,"16a788df-045e-4882-b183-54f5a1eef0ef");var subQ9=sQuery(id+"F0.wireOp",EDGE,"E0.bottom");var subQ11=sQuery(id+"F0.wireOp",EDGE,"E0.right");Q7=makeQuery(id+"FeQxwqO8TE0xPhn_1.1.F6.boolean.opBoolean","INTERSECT",EDGE,{"derivedFrom":[makeQuery(id+"FeQxwqO8TE0xPhn_1.1.F2.boolean.opBoolean","SPLIT",FACE,{"disambiguationData":[TD([makeQuery(id+"F1.opExtrude","SWEPT_FACE",FACE,{"disambiguationData":[OSD([subQ2])]})])],"derivedFrom":makeQuery(id+"F1.opExtrude","CAP_FACE",FACE,{"disambiguationData":[OSD([subQ9,subQ5,subQ2,subQ11,subQ4,subQ3,subQ8,subQ7])],"isStart":false})}),makeQuery(id+"FeQxwqO8TE0xPhn_1.1.F6.opExtrude","CAP_FACE",FACE,{"disambiguationData":[OSD([subQ1,sQuery(id+"F5.wireOp",EDGE,"E19"),sQuery(id+"F5.wireOp",EDGE,"E20"),subQ0,sQuery(id+"F5.wireOp",EDGE,"E22"),sQuery(id+"F5.wireOp",EDGE,"E23")])],"isStart":false})]});}
            fillet(context, id + "F8", {"entities" : qUnion([Q0, Q1, Q2, Q3, Q4, Q5, Q6, Q7]), "radius" : 101.6 * mm, "tangentPropagation" : true, "allowEdgeOverflow" : false});
        }
        {
            var Q0;
            Q0=makeQuery(id+"F2.opExtrude","SWEPT_FACE",FACE,{"disambiguationData":[OSD([sQuery(id+"F0.wireOp",EDGE,"E10")])]});
            var sketch = newSketch(context, id + "F9", { "sketchPlane" : qUnion([Q0])});
            skLineSegment(sketch, "E24", {"start": v(-354.26, 13.15) * mm, "end": v(-382.5, 7.14) * mm});
            skLineSegment(sketch, "E25", {"start": v(-382.5, 7.14) * mm, "end": v(-382.5, -7.14) * mm});
            skLineSegment(sketch, "E26", {"start": v(-382.5, -7.14) * mm, "end": v(-354.26, -13.15) * mm});
            skLineSegment(sketch, "E27", {"start": v(-354.26, -13.15) * mm, "end": v(-341.23, -14.29) * mm});
            skLineSegment(sketch, "E28", {"start": v(-341.23, -14.29) * mm, "end": v(-341.23, 14.29) * mm});
            skLineSegment(sketch, "E29", {"start": v(-341.23, 14.29) * mm, "end": v(-354.26, 13.15) * mm});
            skSolve(sketch);
        }
        {
            var Q0;
            Q0=makeQuery(id+"F9.imprint","IMPRINT",FACE,{"disambiguationData":[TD([[makeQuery(id+"F9.imprint","IMPRINT",EDGE,{"derivedFrom":sQuery(id+"F9.wireOp",EDGE,"E24")}),1.0]])]});
            extrude(context, id + "F10", {"entities" : qUnion([Q0]), "operationType" : NewBodyOperationType.ADD, "oppositeDirection" : true, "depth" : 152 * mm, "offsetDistance" : 25 * mm});
        }
        {
            var Q0;
            Q0=makeQuery(id+"F0.imprint","IMPRINT",FACE,{"disambiguationData":[TD([[makeQuery(id+"F0.imprint","IMPRINT",EDGE,{"derivedFrom":sQuery(id+"F0.wireOp",EDGE,"E5")}),-1.0]])]});
            var Q1;
            Q1=sQuery(id+"F0.wireOp",EDGE,"E8");
            revolve(context, id + "F11", {"operationType" : NewBodyOperationType.REMOVE, "surfaceOperationType" : NewSurfaceOperationType.NEW, "entities" : qUnion([Q0]), "axis" : qUnion([Q1]), "revolveType" : RevolveType.FULL, "oppositeDirection" : true});
        }
        {
            var Q0;
            Q0=makeQuery(id+"F0.imprint","IMPRINT",FACE,{"disambiguationData":[TD([[makeQuery(id+"F0.imprint","IMPRINT",EDGE,{"derivedFrom":sQuery(id+"F0.wireOp",EDGE,"E1")}),-1.0]])]});
            var Q1;
            Q1=sQuery(id+"F0.wireOp",EDGE,"E17");
            revolve(context, id + "F12", {"operationType" : NewBodyOperationType.REMOVE, "surfaceOperationType" : NewSurfaceOperationType.NEW, "entities" : qUnion([Q0]), "axis" : qUnion([Q1]), "revolveType" : RevolveType.FULL, "oppositeDirection" : true});
        }
        {
            var Q0;
            {var subQ0=sQuery(id+"F5.wireOp",EDGE,"E18");Q0=makeQuery(id+"FeQxwqO8TE0xPhn_1.3.F6.boolean.opBoolean","MERGE",FACE,{"derivedFrom":[makeQuery(id+"FeQxwqO8TE0xPhn_1.2.F6.boolean.opBoolean","MERGE",FACE,{"derivedFrom":[makeQuery(id+"FeQxwqO8TE0xPhn_1.1.F6.boolean.opBoolean","MERGE",FACE,{"derivedFrom":[makeQuery(id+"F6.boolean.opBoolean","MERGE",FACE,{"derivedFrom":[makeQuery(id+"F1.opExtrude","SWEPT_FACE",FACE,{"disambiguationData":[OSD([sQuery(id+"F0.wireOp",EDGE,"E0.top"),sQuery(id+"F0.wireOp",EDGE,"E2"),sQuery(id+"F0.wireOp",EDGE,"E3")])]}),makeQuery(id+"F6.opExtrude","SWEPT_FACE",FACE,{"disambiguationData":[OSD([subQ0])]})]}),makeQuery(id+"FeQxwqO8TE0xPhn_1.1.F6.opExtrude","SWEPT_FACE",FACE,{"disambiguationData":[OSD([subQ0])]})]}),makeQuery(id+"FeQxwqO8TE0xPhn_1.2.F6.opExtrude","SWEPT_FACE",FACE,{"disambiguationData":[OSD([subQ0])]})]}),makeQuery(id+"FeQxwqO8TE0xPhn_1.3.F6.opExtrude","SWEPT_FACE",FACE,{"disambiguationData":[OSD([subQ0])]})]});}
            var sketch = newSketch(context, id + "F13", { "sketchPlane" : qUnion([Q0])});
            skCircle(sketch, "E30", {"center": v(-83.07, 83.07) * mm, "radius": 9.53 * mm});
            skCircle(sketch, "E31", {"center": v(83.07, -83.07) * mm, "radius": 9.53 * mm});
            skLineSegment(sketch, "E32", {"start": v(-83.07, 83.07) * mm, "end": v(83.07, -83.07) * mm, "construction": true});
            skLineSegment(sketch, "E33", {"start": v(0, 0) * mm, "end": v(91.32, 0) * mm, "construction": true});
            skPoint(sketch, "E34", {"position": v(0, 0) * mm});
            skLineSegment(sketch, "E35", {"start": v(33.87, 51.83) * mm, "end": v(39.29, 57.25) * mm});
            skLineSegment(sketch, "E36", {"start": v(39.29, 57.25) * mm, "end": v(57.25, 39.29) * mm});
            skLineSegment(sketch, "E37", {"start": v(57.25, 39.29) * mm, "end": v(51.83, 33.87) * mm});
            skSolve(sketch);
        }
        {
            var Q0;
            Q0=makeQuery(id+"F13.imprint","IMPRINT",FACE,{"disambiguationData":[TD([[makeQuery(id+"F13.imprint","IMPRINT",EDGE,{"derivedFrom":sQuery(id+"F13.wireOp",EDGE,"E30")}),1.0]])]});
            var Q1;
            Q1=makeQuery(id+"F13.imprint","IMPRINT",FACE,{"disambiguationData":[TD([[makeQuery(id+"F13.imprint","IMPRINT",EDGE,{"derivedFrom":sQuery(id+"F13.wireOp",EDGE,"E31")}),1.0]])]});
            var Q2;
            {var subQ0=sQuery(id+"F13.wireOp",EDGE,"E35");Q2=makeQuery(id+"F13.imprint","IMPRINT",FACE,{"disambiguationData":[TD([[makeQuery(id+"F13.imprint","IMPRINT",EDGE,{"derivedFrom":subQ0}),-1.0]])]});}
            extrude(context, id + "F14", {"entities" : qUnion([Q0, Q1, Q2]), "operationType" : NewBodyOperationType.REMOVE, "endBound" : BoundingType.THROUGH_ALL, "oppositeDirection" : true, "depth" : 25 * mm, "offsetDistance" : 25 * mm});
        }
    });
